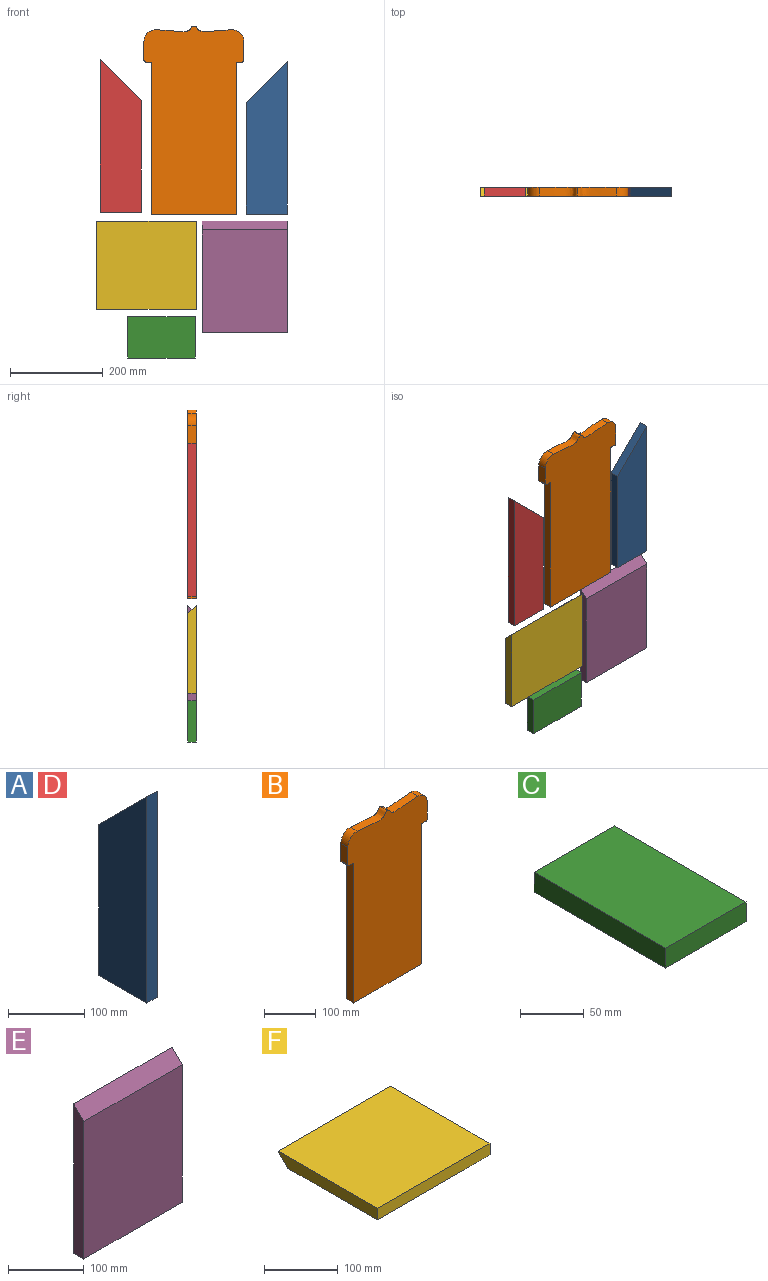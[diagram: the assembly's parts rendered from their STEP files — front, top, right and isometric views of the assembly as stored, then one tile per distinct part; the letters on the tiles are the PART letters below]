
ASSEMBLY  parts=6 mates=5
PART A: 6 faces, bbox 19.1x88.9x330.2 mm
  f0: plane 330.2x19.05mm, normal (0,-1,0), area 6290.3mm2, adj f1,f3,f4,f5
  f1: plane 88.9x19.05mm, normal (0,0,-1), area 1693.5mm2, adj f0,f2,f4,f5
  f2: plane 241.3x19.05mm, normal (0,1,0), area 4596.8mm2, adj f1,f3,f4,f5
  f3: plane 88.9x88.9mm, normal (0,0.71,0.71), area 2395mm2, adj f0,f2,f4,f5
  f4: plane 330.2x88.9mm, normal (1,0,0), area 25403.2mm2, adj f0,f1,f2,f3
  f5: plane 330.2x88.9mm, normal (-1,0,0), area 25403.2mm2, adj f0,f1,f2,f3
PART B: 17 faces, bbox 215.9x19.1x408 mm
  f0: plane 327.03x19.05mm, normal (1,0,0), area 6229.8mm2, adj f2,f3,f4,f15
  f1: plane 327.03x19.05mm, normal (-1,0,0), area 6229.8mm2, adj f2,f3,f4,f16
  f2: plane 184.15x19.05mm, normal (0,0,-1), area 3508.1mm2, adj f0,f1,f3,f4
  f3: plane 408x215.9mm, normal (0,-1,0), area 75355.3mm2, adj f0,f1,f2,f5,f6,f7,f8,f9
  f4: plane 408x215.9mm, normal (0,1,0), area 75355.3mm2, adj f0,f1,f2,f5,f6,f7,f8,f9
  f5: plane 19.05x9.53mm, normal (0,0,-1), area 181.5mm2, adj f3,f4,f13,f15
  f6: plane 41.28x19.05mm, normal (1,0,0), area 786.3mm2, adj f3,f4,f7,f13
  f7: cylinder r=25.4mm len=25.4mm, axis (0,-1,0), area 760.1mm2, adj f3,f4,f6,f8
  f8: extruded ~82.55x19.05mm, area 1664.1mm2, adj f3,f4,f7,f9
  f9: extruded ~82.55x19.05mm, area 1664.1mm2, adj f3,f4,f8,f11
  f10: plane 19.05x9.53mm, normal (0,0,-1), area 181.5mm2, adj f3,f4,f14,f16
  f11: cylinder r=25.4mm len=25.4mm, axis (0,-1,0), area 760.1mm2, adj f3,f4,f9,f12
  f12: plane 41.28x19.05mm, normal (-1,0,0), area 786.3mm2, adj f3,f4,f11,f14
  f13: cylinder r=3.17mm len=19.05mm, axis (0,-1,0), area 95mm2, adj f3,f4,f5,f6
  f14: cylinder r=3.17mm len=19.05mm, axis (0,-1,0), area 95mm2, adj f3,f4,f10,f12
  f15: cylinder r=3.17mm len=19.05mm, axis (0,1,0), area 95mm2, adj f0,f3,f4,f5
  f16: cylinder r=3.17mm len=19.05mm, axis (0,-1,0), area 95mm2, adj f1,f3,f4,f10
PART C: 6 faces, bbox 88.9x146.1x19.1 mm
  f0: plane 146.05x19.05mm, normal (1,0,0), area 2782.3mm2, adj f1,f3,f4,f5
  f1: plane 88.9x19.05mm, normal (0,1,0), area 1693.5mm2, adj f0,f2,f4,f5
  f2: plane 146.05x19.05mm, normal (-1,0,0), area 2782.3mm2, adj f1,f3,f4,f5
  f3: plane 88.9x19.05mm, normal (0,-1,0), area 1693.5mm2, adj f0,f2,f4,f5
  f4: plane 146.05x88.9mm, normal (0,0,1), area 12983.8mm2, adj f0,f1,f2,f3
  f5: plane 146.05x88.9mm, normal (0,0,-1), area 12983.8mm2, adj f0,f1,f2,f3
PART D: same geometry as A
PART E: 6 faces, bbox 184.2x19.1x241.3 mm
  f0: plane 241.3x19.05mm, normal (1,0,0), area 4415.3mm2, adj f2,f3,f4,f5
  f1: plane 241.3x19.05mm, normal (-1,0,0), area 4415.3mm2, adj f2,f3,f4,f5
  f2: plane 184.15x19.05mm, normal (0,0,-1), area 3508.1mm2, adj f0,f1,f3,f4
  f3: plane 222.25x184.15mm, normal (0,-1,0), area 40927.3mm2, adj f0,f1,f2,f5
  f4: plane 241.3x184.15mm, normal (0,1,0), area 44435.4mm2, adj f0,f1,f2,f5
  f5: plane 184.15x19.05mm, normal (0,-0.71,0.71), area 4961.1mm2, adj f0,f1,f3,f4
PART F: 6 faces, bbox 215.9x190.5x19.1 mm
  f0: plane 190.5x19.05mm, normal (1,0,0), area 3447.6mm2, adj f2,f3,f4,f5
  f1: plane 190.5x19.05mm, normal (-1,0,0), area 3447.6mm2, adj f2,f3,f4,f5
  f2: plane 215.9x19.05mm, normal (0,-1,0), area 4112.9mm2, adj f0,f1,f3,f4
  f3: plane 215.9x190.5mm, normal (0,0,1), area 41129mm2, adj f0,f1,f2,f5
  f4: plane 215.9x171.45mm, normal (0,0,-1), area 37016.1mm2, adj f0,f1,f2,f5
  f5: plane 215.9x19.05mm, normal (0,0.71,-0.71), area 5816.5mm2, adj f0,f1,f3,f4
PLACE A rot(axis=(0,0,1),90deg) t=(157.47,-19.05,1.72)mm
PLACE B at identity fixed
PLACE C rot(axis=(0.58,0.58,-0.58),120deg) t=(-70.21,0,-429.93)mm
PLACE D rot(axis=(0,0,-1),90deg) t=(-157.78,0,5.58)mm
PLACE E t=(110,0,-299.36)mm
PLACE F rot(axis=(1,0,0),90deg) t=(-102.56,0,-274.09)mm
MATE planar E.f3 <-> F.f3  axis (0,-1,0) through (110,-19.05,-308.88)mm
MATE planar E.f3 <-> A.f5  axis (0,-1,0) through (110,-19.05,-308.88)mm
MATE planar D.f4 <-> E.f3  axis (0,-1,0) through (-160.09,-19.05,-15.49)mm
MATE planar C.f4 <-> B.f3  axis (0,-1,0) through (-70.21,-19.05,-429.93)mm
MATE planar F.f3 <-> B.f3  axis (0,-1,0) through (-102.56,-19.05,-274.09)mm
